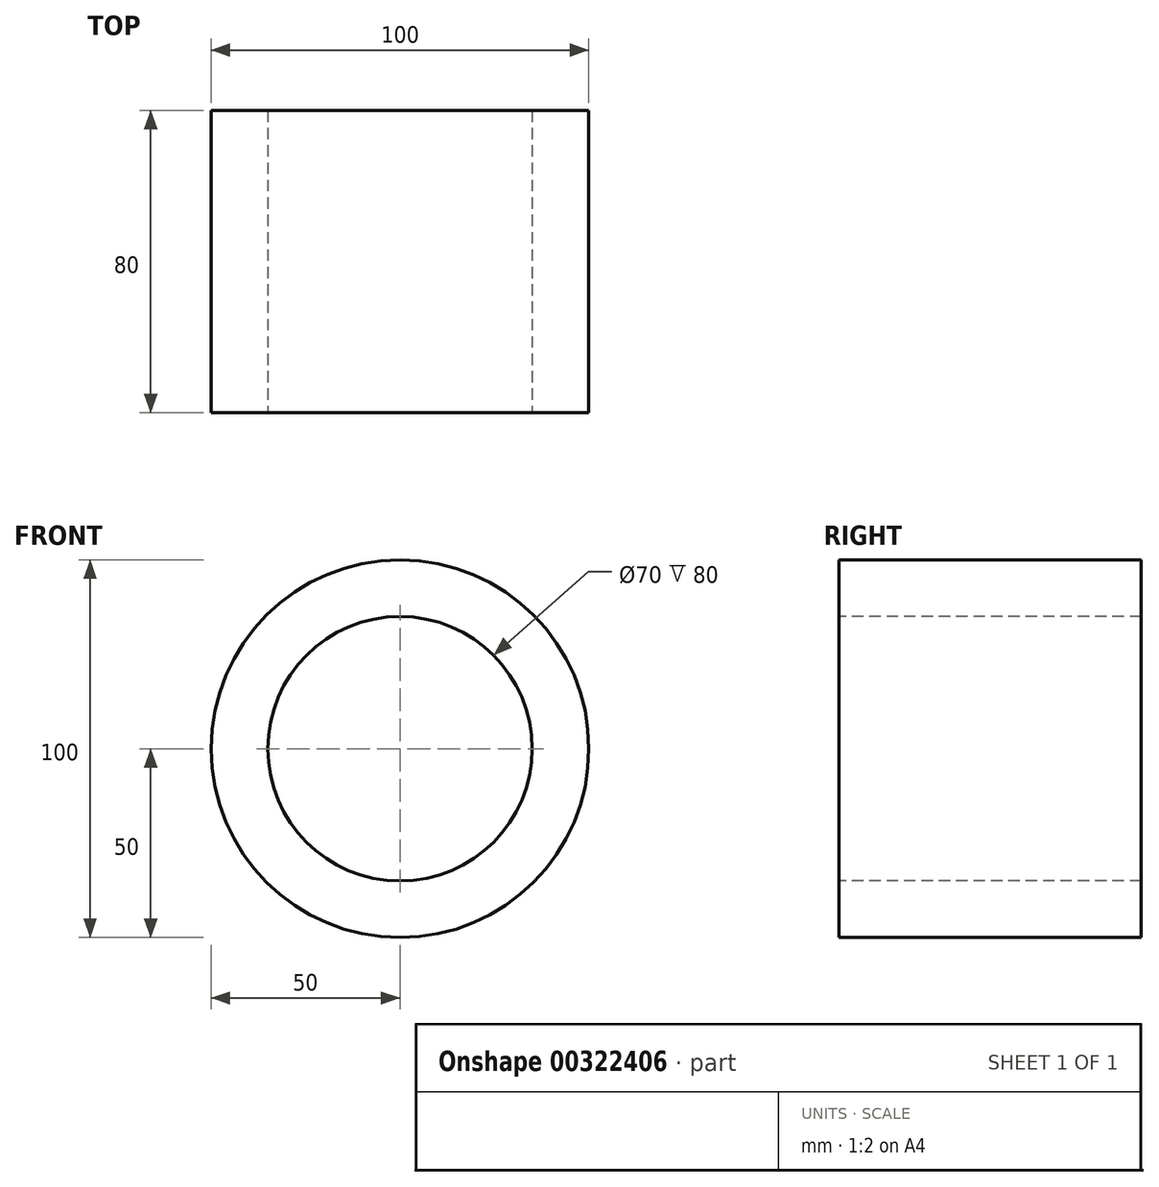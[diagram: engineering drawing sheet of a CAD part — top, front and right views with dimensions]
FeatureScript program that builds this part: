
annotation { "Feature Type Name" : "Feature", "Feature Type Description" : "" }
export const myFeature = defineFeature(function(context is Context, id is Id, definition is map)
    precondition{}
    {
        {
            var Q0;
            Q0=qCreatedBy(makeId("Front.planeOp"),FACE);
            var sketch = newSketch(context, id + "F0", { "sketchPlane" : qUnion([Q0])});
            skCircle(sketch, "E0", {"center": v(0, 0) * mm, "radius": 50 * mm});
            skSolve(sketch);
        }
        {
            var Q0;
            Q0=makeQuery(id+"F0.imprint","IMPRINT",FACE,{"disambiguationData":[TD([[makeQuery(id+"F0.imprint","IMPRINT",EDGE,{"derivedFrom":sQuery(id+"F0.wireOp",EDGE,"E0")}),1.0]])]});
            extrude(context, id + "F1", {"entities" : qUnion([Q0]), "depth" : 80 * mm});
        }
        {
            var Q0;
            Q0=makeQuery(id+"F1.opExtrude","CAP_FACE",FACE,{"disambiguationData":[OSD([sQuery(id+"F0.wireOp",EDGE,"E0")])],"isStart":false});
            var sketch = newSketch(context, id + "F2", { "sketchPlane" : qUnion([Q0])});
            skCircle(sketch, "E1", {"center": v(0, 0) * mm, "radius": 35 * mm});
            skSolve(sketch);
        }
        {
            var Q0;
            Q0=makeQuery(id+"F2.imprint","IMPRINT",FACE,{"disambiguationData":[TD([[makeQuery(id+"F2.imprint","IMPRINT",EDGE,{"derivedFrom":sQuery(id+"F2.wireOp",EDGE,"E1")}),1.0]])]});
            extrude(context, id + "F3", {"entities" : qUnion([Q0]), "operationType" : NewBodyOperationType.REMOVE, "endBound" : BoundingType.UP_TO_NEXT, "oppositeDirection" : true, "depth" : 25 * mm});
        }
    });
